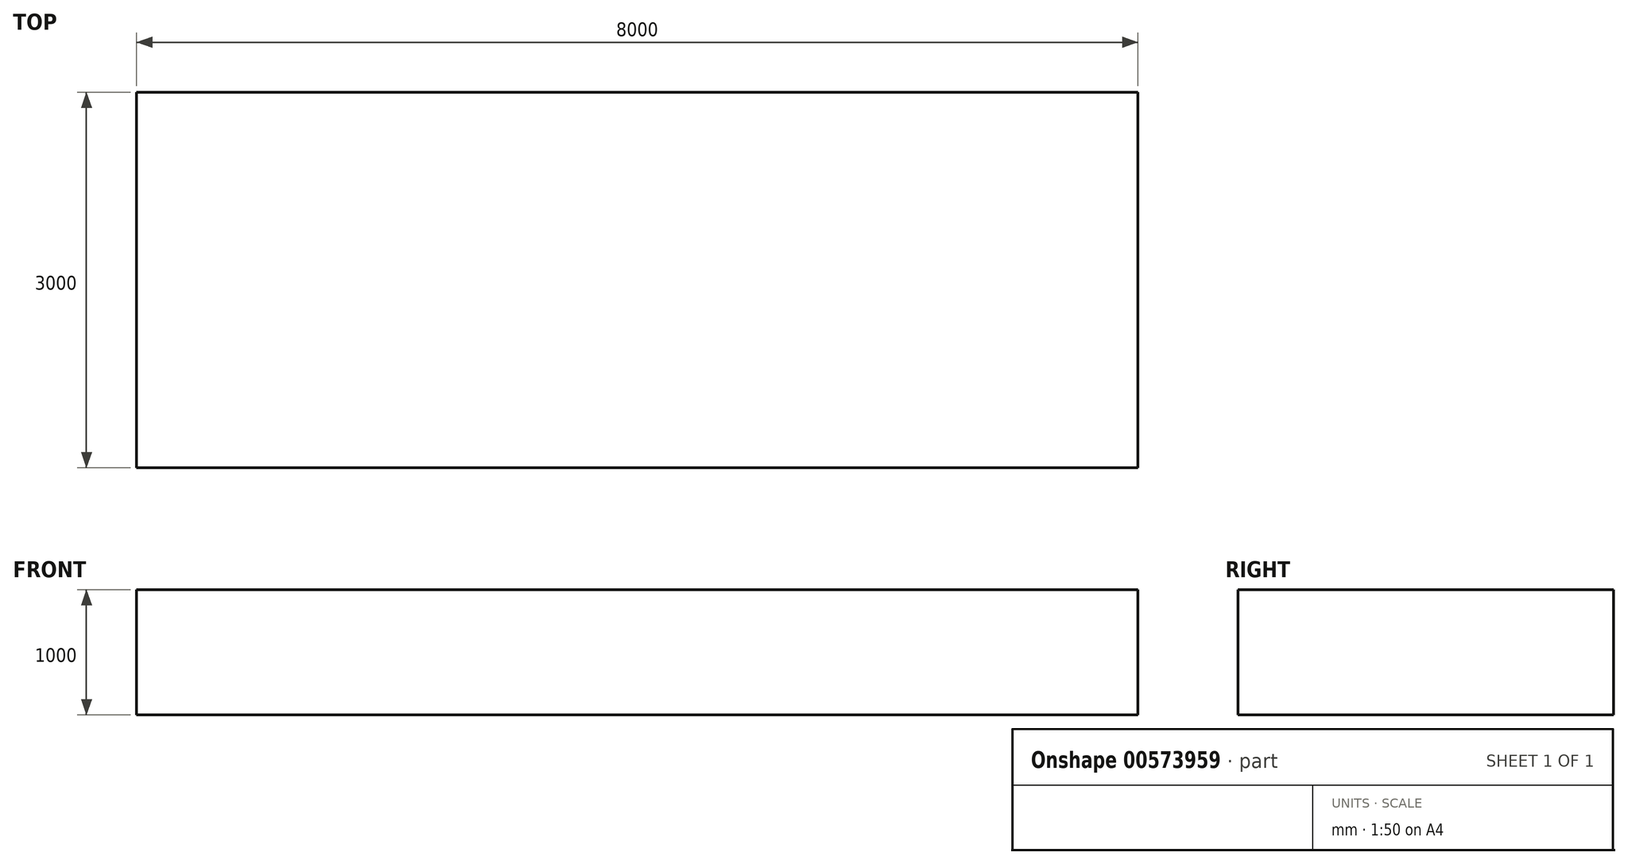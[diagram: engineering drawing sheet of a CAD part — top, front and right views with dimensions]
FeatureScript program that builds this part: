
annotation { "Feature Type Name" : "Feature", "Feature Type Description" : "" }
export const myFeature = defineFeature(function(context is Context, id is Id, definition is map)
    precondition{}
    {
        {
            var Q0;
            Q0=qCreatedBy(makeId("Top.planeOp"),FACE);
            var sketch = newSketch(context, id + "F0", { "sketchPlane" : qUnion([Q0])});
            skLineSegment(sketch, "E0.bottom", {"start": v(4000, 1500) * mm, "end": v(-4000, 1500) * mm});
            skLineSegment(sketch, "E0.top", {"start": v(4000, -1500) * mm, "end": v(-4000, -1500) * mm});
            skLineSegment(sketch, "E0.left", {"start": v(4000, 1500) * mm, "end": v(4000, -1500) * mm});
            skLineSegment(sketch, "E0.right", {"start": v(-4000, 1500) * mm, "end": v(-4000, -1500) * mm});
            skPoint(sketch, "E0.middle", {"position": v(0, 0) * mm});
            skSolve(sketch);
        }
        {
            var Q0;
            Q0 = qSketchRegion(id + "F0", true);
            extrude(context, id + "F1", {"entities" : qUnion([Q0]), "depth" : 1000 * mm, "offsetDistance" : 25 * mm});
        }
    });
